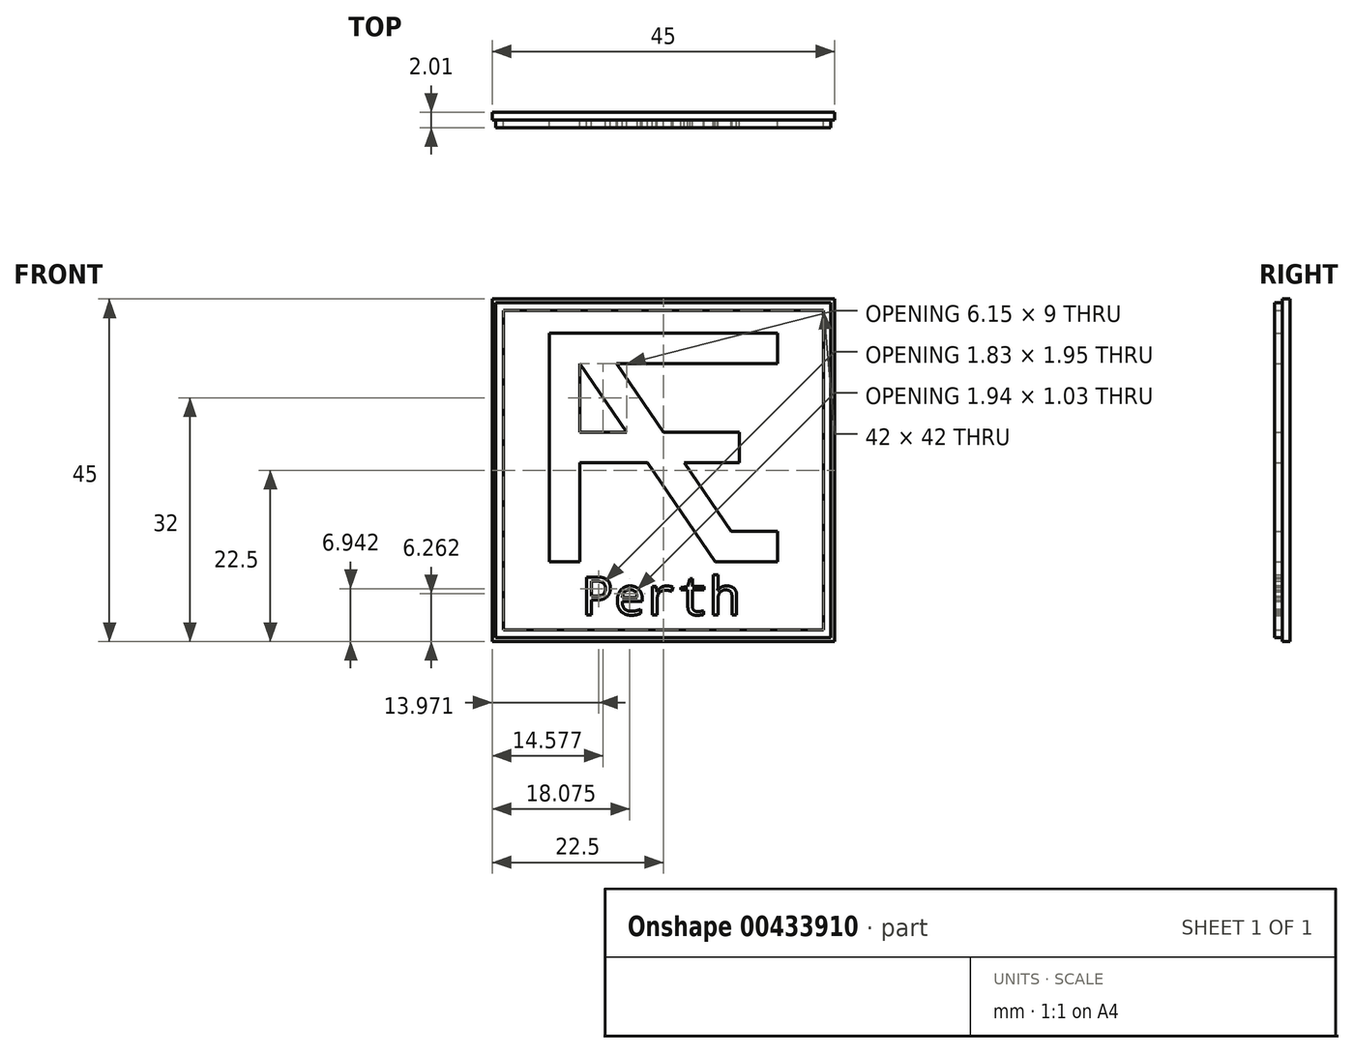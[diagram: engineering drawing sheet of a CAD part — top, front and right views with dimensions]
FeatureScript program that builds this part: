
annotation { "Feature Type Name" : "Feature", "Feature Type Description" : "" }
export const myFeature = defineFeature(function(context is Context, id is Id, definition is map)
    precondition{}
    {
        {
            var Q0;
            Q0=qCreatedBy(makeId("Front.planeOp"),FACE);
            var sketch = newSketch(context, id + "F0", { "sketchPlane" : qUnion([Q0])});
            skLineSegment(sketch, "E0.bottom", {"start": v(22.5, -25.5) * mm, "end": v(-22.5, -25.5) * mm});
            skLineSegment(sketch, "E0.top", {"start": v(22.5, 19.5) * mm, "end": v(-22.5, 19.5) * mm});
            skLineSegment(sketch, "E0.left", {"start": v(22.5, -25.5) * mm, "end": v(22.5, 19.5) * mm});
            skLineSegment(sketch, "E0.right", {"start": v(-22.5, -25.5) * mm, "end": v(-22.5, 19.5) * mm});
            skPoint(sketch, "E0.middle", {"position": v(0, -3) * mm});
            skSolve(sketch);
        }
        {
            var Q0;
            Q0 = qSketchRegion(id + "F0", true);
            extrude(context, id + "F1", {"entities" : qUnion([Q0]), "depth" : 1 * mm});
        }
        {
            var Q0;
            Q0=qCreatedBy(makeId("Front.planeOp"),FACE);
            cPlane(context, id + "F2", {"entities" : qUnion([Q0]), "cplaneType" : CPlaneType.OFFSET, "offset" : 1.01 * mm, "width" : 150 * mm, "height" : 150 * mm});
        }
        {
            var Q0;
            Q0=qCreatedBy(id+"F2.planeOp",FACE);
            var sketch = newSketch(context, id + "F3", { "sketchPlane" : qUnion([Q0])});
            skLineSegment(sketch, "E1", {"start": v(-15, 15) * mm, "end": v(-15, -15) * mm});
            skLineSegment(sketch, "E2", {"start": v(-15, -15) * mm, "end": v(-11, -15) * mm});
            skLineSegment(sketch, "E3", {"start": v(-11, -15) * mm, "end": v(-11, -2) * mm});
            skLineSegment(sketch, "E4", {"start": v(-11, -2) * mm, "end": v(-2.11, -2) * mm});
            skLineSegment(sketch, "E5", {"start": v(-2.11, -2) * mm, "end": v(6.78, -15) * mm});
            skLineSegment(sketch, "E6", {"start": v(6.78, -15) * mm, "end": v(15, -15) * mm});
            skLineSegment(sketch, "E7", {"start": v(-15, 15) * mm, "end": v(15, 15) * mm});
            skLineSegment(sketch, "E8", {"start": v(15, 15) * mm, "end": v(15, 11) * mm});
            skLineSegment(sketch, "E9", {"start": v(15, 11) * mm, "end": v(-6.15, 11) * mm});
            skLineSegment(sketch, "E10", {"start": v(-6.15, 11) * mm, "end": v(0, 2) * mm});
            skLineSegment(sketch, "E11", {"start": v(0, 2) * mm, "end": v(10, 2) * mm});
            skLineSegment(sketch, "E12", {"start": v(10, 2) * mm, "end": v(10, -2) * mm});
            skLineSegment(sketch, "E13", {"start": v(10, -2) * mm, "end": v(2.74, -2) * mm});
            skLineSegment(sketch, "E14", {"start": v(2.74, -2) * mm, "end": v(8.89, -11) * mm});
            skLineSegment(sketch, "E15", {"start": v(8.89, -11) * mm, "end": v(15, -11) * mm});
            skLineSegment(sketch, "E16", {"start": v(-11, 2) * mm, "end": v(-11, 11) * mm});
            skLineSegment(sketch, "E17", {"start": v(-11, 11) * mm, "end": v(-4.85, 2) * mm});
            skLineSegment(sketch, "E18", {"start": v(-4.85, 2) * mm, "end": v(-11, 2) * mm});
            skLineSegment(sketch, "E19", {"start": v(15, -11) * mm, "end": v(15, -15) * mm});
            skText(sketch, "E20", { "text": "Perth", "fontName": "DroidSansMono.ttf"});
            skPoint(sketch, "E21.middle", {"position": v(0, 0) * mm});
            const initialGuessF3  = {"E20": [-0.01067, -0.022, 1, 0, 0.005]};
            skSetInitialGuess(sketch, initialGuessF3);
            skSolve(sketch);
        }
        {
            var Q0;
            Q0 = qSketchRegion(id + "F3", true);
            extrude(context, id + "F4", {"entities" : qUnion([Q0]), "operationType" : NewBodyOperationType.ADD, "depth" : 1 * mm});
        }
        {
            var Q0;
            Q0=qCreatedBy(id+"F2.planeOp",FACE);
            var sketch = newSketch(context, id + "F5", { "sketchPlane" : qUnion([Q0])});
            skLineSegment(sketch, "E22.bottom", {"start": v(-21, 18) * mm, "end": v(21, 18) * mm});
            skLineSegment(sketch, "E22.top", {"start": v(-21, -24) * mm, "end": v(21, -24) * mm});
            skLineSegment(sketch, "E22.left", {"start": v(-21, 18) * mm, "end": v(-21, -24) * mm});
            skLineSegment(sketch, "E22.right", {"start": v(21, 18) * mm, "end": v(21, -24) * mm});
            skPoint(sketch, "E22.middle", {"position": v(0, -3) * mm});
            skLineSegment(sketch, "E23.bottom", {"start": v(-22, 19) * mm, "end": v(22, 19) * mm});
            skLineSegment(sketch, "E23.top", {"start": v(-22, -25) * mm, "end": v(22, -25) * mm});
            skLineSegment(sketch, "E23.left", {"start": v(-22, 19) * mm, "end": v(-22, -25) * mm});
            skLineSegment(sketch, "E23.right", {"start": v(22, 19) * mm, "end": v(22, -25) * mm});
            skSolve(sketch);
        }
        {
            var Q0;
            Q0 = qSketchRegion(id + "F5", true);
            extrude(context, id + "F6", {"entities" : qUnion([Q0]), "operationType" : NewBodyOperationType.ADD, "depth" : 1 * mm});
        }
    });
